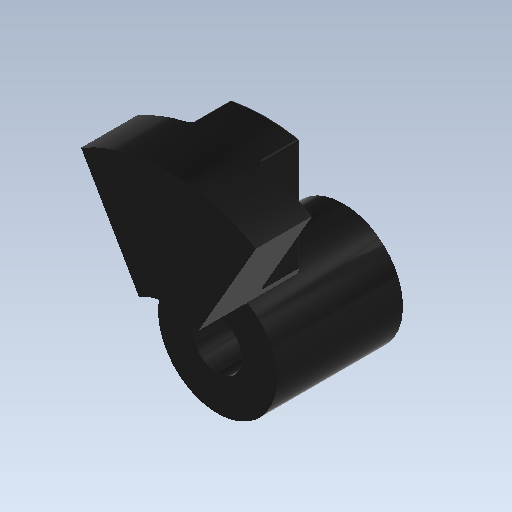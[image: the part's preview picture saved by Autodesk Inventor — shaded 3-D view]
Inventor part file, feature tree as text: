
AUTODESK INVENTOR PART (.ipt)
format: ipt  version: 2020 (Build 240168000, 168)  size: 154,624 bytes
history: native  units: mm
features: sketch x3, extrude x2, other x1, revolve x1, fillet x1, projected_geometry x1
ambient origin geometry x8: Origin, YZ Plane, XZ Plane, XY Plane, X Axis, Y Axis, Z Axis, Center Point
bodies: Body1 (feature_tree)
feature tree (9):
  other  "Твердое тело1"
  revolve  "Вращение1"
  extrude  "Выдавливание1"  Depth=5.0mm
  extrude  "Выдавливание2"  Depth=1.4mm
  fillet  "Сопряжение1"  Radius=3.4mm
  sketch  "Эскиз1"
  sketch  "Эскиз2"
  sketch  "Эскиз3"
  projected_geometry  "Спроецированная петля1"
